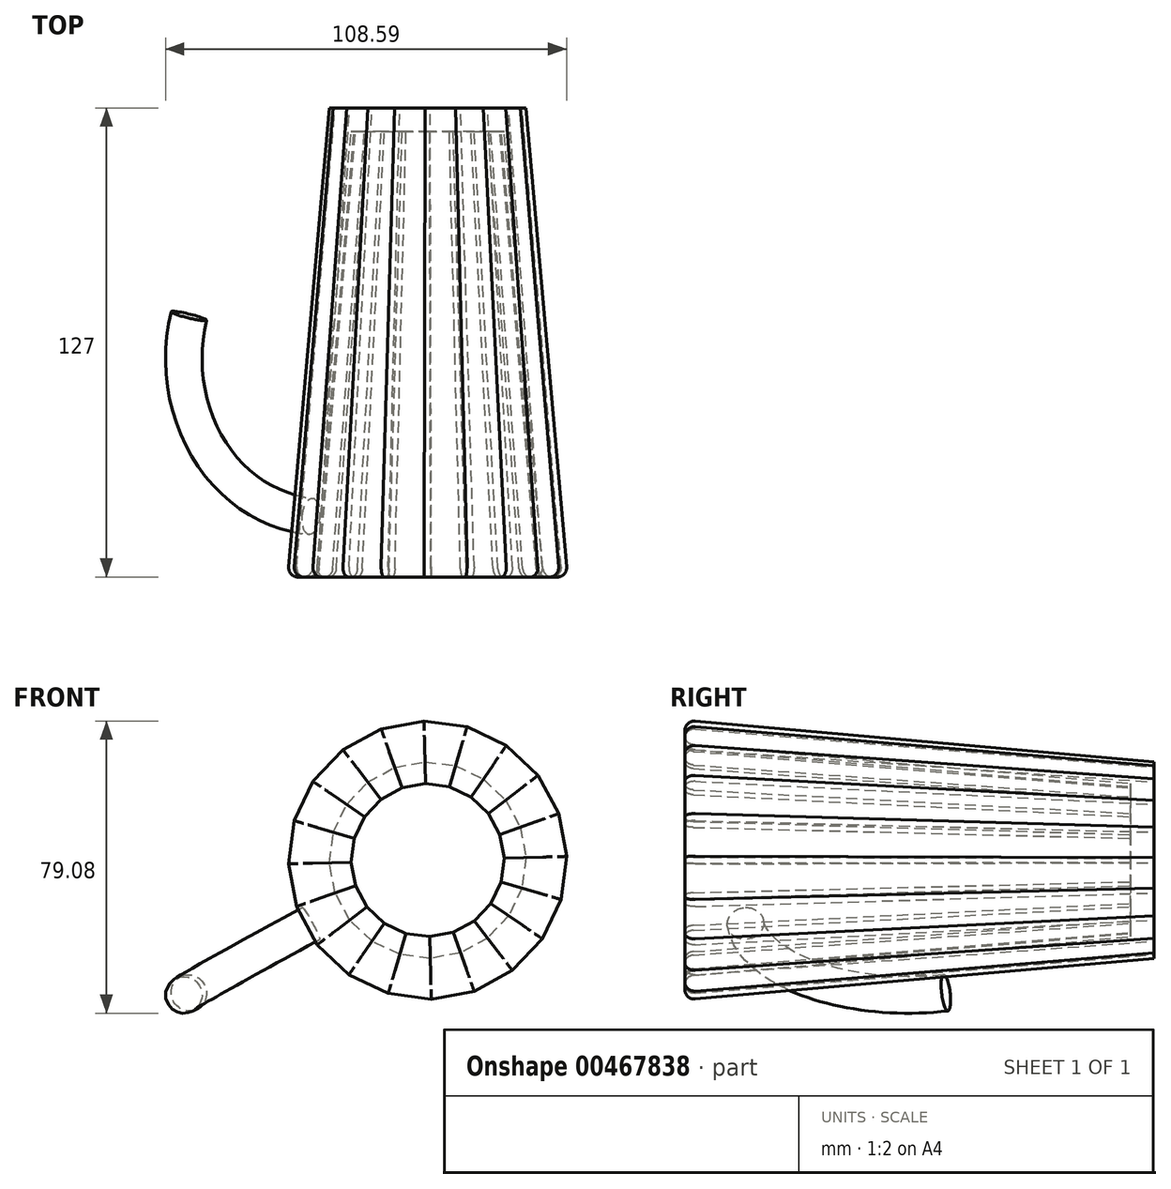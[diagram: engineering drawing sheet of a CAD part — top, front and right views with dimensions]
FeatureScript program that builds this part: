
annotation { "Feature Type Name" : "Feature", "Feature Type Description" : "" }
export const myFeature = defineFeature(function(context is Context, id is Id, definition is map)
    precondition{}
    {
        {
            var Q0;
            Q0=qCreatedBy(makeId("Front.planeOp"),FACE);
            var sketch = newSketch(context, id + "F0", { "sketchPlane" : qUnion([Q0])});
            skCircle(sketch, "E0.cCircle", {"center": v(0, 0) * mm, "radius": 26.3 * mm, "construction": true});
            skLineSegment(sketch, "E0.0", {"start": v(0.7, -26.62) * mm, "end": v(-7.55, -25.53) * mm});
            skLineSegment(sketch, "E0.1", {"start": v(-7.55, -25.53) * mm, "end": v(-15.07, -21.95) * mm});
            skLineSegment(sketch, "E0.2", {"start": v(-15.07, -21.95) * mm, "end": v(-21.12, -16.22) * mm});
            skLineSegment(sketch, "E0.3", {"start": v(-21.12, -16.22) * mm, "end": v(-25.1, -8.9) * mm});
            skLineSegment(sketch, "E0.4", {"start": v(-25.1, -8.9) * mm, "end": v(-26.62, -0.7) * mm});
            skLineSegment(sketch, "E0.5", {"start": v(-26.62, -0.7) * mm, "end": v(-25.53, 7.55) * mm});
            skLineSegment(sketch, "E0.6", {"start": v(-25.53, 7.55) * mm, "end": v(-21.95, 15.07) * mm});
            skLineSegment(sketch, "E0.7", {"start": v(-21.95, 15.07) * mm, "end": v(-16.22, 21.12) * mm});
            skLineSegment(sketch, "E0.8", {"start": v(-16.22, 21.12) * mm, "end": v(-8.9, 25.1) * mm});
            skLineSegment(sketch, "E0.9", {"start": v(-8.9, 25.1) * mm, "end": v(-0.7, 26.62) * mm});
            skLineSegment(sketch, "E0.10", {"start": v(-0.7, 26.62) * mm, "end": v(7.55, 25.53) * mm});
            skLineSegment(sketch, "E0.11", {"start": v(7.55, 25.53) * mm, "end": v(15.07, 21.95) * mm});
            skLineSegment(sketch, "E0.12", {"start": v(15.07, 21.95) * mm, "end": v(21.12, 16.22) * mm});
            skLineSegment(sketch, "E0.13", {"start": v(21.12, 16.22) * mm, "end": v(25.1, 8.9) * mm});
            skLineSegment(sketch, "E0.14", {"start": v(25.1, 8.9) * mm, "end": v(26.62, 0.7) * mm});
            skLineSegment(sketch, "E0.15", {"start": v(26.62, 0.7) * mm, "end": v(25.53, -7.55) * mm});
            skLineSegment(sketch, "E0.16", {"start": v(25.53, -7.55) * mm, "end": v(21.95, -15.07) * mm});
            skLineSegment(sketch, "E0.17", {"start": v(21.95, -15.07) * mm, "end": v(16.22, -21.12) * mm});
            skLineSegment(sketch, "E0.18", {"start": v(16.22, -21.12) * mm, "end": v(8.9, -25.1) * mm});
            skLineSegment(sketch, "E0.19", {"start": v(8.9, -25.1) * mm, "end": v(0.7, -26.62) * mm});
            skPoint(sketch, "E0.0.midPoint", {"position": v(-3.42, -26.08) * mm});
            skSolve(sketch);
        }
        {
            var Q0;
            Q0 = qSketchRegion(id + "F0", true);
            extrude(context, id + "F1", {"entities" : qUnion([Q0]), "depth" : 127 * mm, "hasDraft" : true, "draftAngle" : 5 * degree});
        }
        {
            var Q0;
            Q0=makeQuery(id+"F1.opExtrude","CAP_FACE",FACE,{"disambiguationData":[OSD([sQuery(id+"F0.wireOp",EDGE,"E0.0"),sQuery(id+"F0.wireOp",EDGE,"E0.1"),sQuery(id+"F0.wireOp",EDGE,"E0.2"),sQuery(id+"F0.wireOp",EDGE,"E0.3"),sQuery(id+"F0.wireOp",EDGE,"E0.4"),sQuery(id+"F0.wireOp",EDGE,"E0.5"),sQuery(id+"F0.wireOp",EDGE,"E0.6"),sQuery(id+"F0.wireOp",EDGE,"E0.7"),sQuery(id+"F0.wireOp",EDGE,"E0.8"),sQuery(id+"F0.wireOp",EDGE,"E0.9"),sQuery(id+"F0.wireOp",EDGE,"E0.10"),sQuery(id+"F0.wireOp",EDGE,"E0.11"),sQuery(id+"F0.wireOp",EDGE,"E0.12"),sQuery(id+"F0.wireOp",EDGE,"E0.13"),sQuery(id+"F0.wireOp",EDGE,"E0.14"),sQuery(id+"F0.wireOp",EDGE,"E0.15"),sQuery(id+"F0.wireOp",EDGE,"E0.16"),sQuery(id+"F0.wireOp",EDGE,"E0.17"),sQuery(id+"F0.wireOp",EDGE,"E0.18"),sQuery(id+"F0.wireOp",EDGE,"E0.19")])],"isStart":false});
            shell(context, id + "F2", {"entities" : qUnion([Q0]), "thickness" : 6.35 * mm});
        }
        {
            var Q0;
            Q0=makeQuery(id+"F1.opExtrude","SWEPT_FACE",FACE,{"disambiguationData":[OSD([sQuery(id+"F0.wireOp",EDGE,"E0.3")])]});
            var sketch = newSketch(context, id + "F3", { "sketchPlane" : qUnion([Q0])});
            skCircle(sketch, "E1", {"center": v(113.29, 0) * mm, "radius": 4.94 * mm});
            skLineSegment(sketch, "E2", {"start": v(69.86, 14.17) * mm, "end": v(70.28, -16.42) * mm});
            skSolve(sketch);
        }
        {
            var Q0;
            Q0 = qSketchRegion(id + "F3", true);
            var Q1;
            Q1=sQuery(id+"F3.wireOp",EDGE,"E2");
            revolve(context, id + "F4", {"operationType" : NewBodyOperationType.ADD, "entities" : qUnion([Q0]), "axis" : qUnion([Q1]), "revolveType" : RevolveType.ONE_DIRECTION, "angle" : 100 * degree});
        }
        {
            var Q0;
            Q0=makeQuery(id+"F1.opExtrude","CAP_FACE",FACE,{"disambiguationData":[OSD([sQuery(id+"F0.wireOp",EDGE,"E0.0"),sQuery(id+"F0.wireOp",EDGE,"E0.1"),sQuery(id+"F0.wireOp",EDGE,"E0.2"),sQuery(id+"F0.wireOp",EDGE,"E0.3"),sQuery(id+"F0.wireOp",EDGE,"E0.4"),sQuery(id+"F0.wireOp",EDGE,"E0.5"),sQuery(id+"F0.wireOp",EDGE,"E0.6"),sQuery(id+"F0.wireOp",EDGE,"E0.7"),sQuery(id+"F0.wireOp",EDGE,"E0.8"),sQuery(id+"F0.wireOp",EDGE,"E0.9"),sQuery(id+"F0.wireOp",EDGE,"E0.10"),sQuery(id+"F0.wireOp",EDGE,"E0.11"),sQuery(id+"F0.wireOp",EDGE,"E0.12"),sQuery(id+"F0.wireOp",EDGE,"E0.13"),sQuery(id+"F0.wireOp",EDGE,"E0.14"),sQuery(id+"F0.wireOp",EDGE,"E0.15"),sQuery(id+"F0.wireOp",EDGE,"E0.16"),sQuery(id+"F0.wireOp",EDGE,"E0.17"),sQuery(id+"F0.wireOp",EDGE,"E0.18"),sQuery(id+"F0.wireOp",EDGE,"E0.19")])],"isStart":false});
            fillet(context, id + "F5", {"entities" : qUnion([Q0]), "radius" : 2.54 * mm, "tangentPropagation" : true, "allowEdgeOverflow" : false});
        }
    });
